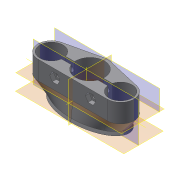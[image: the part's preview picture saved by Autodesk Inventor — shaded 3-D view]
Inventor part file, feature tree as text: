
AUTODESK INVENTOR PART (.ipt)
format: ipt  version: 2015 SP2 (Build 190223200, 223)  size: 519,680 bytes
history: native  units: mm
features: sketch x10, other x6, extrude x6, plane x3, loft x2, mirror x2
ambient origin geometry x8: Origin, YZ Plane, XZ Plane, XY Plane, X Axis, Y Axis, Z Axis, Center Point
bodies: Body1 (feature_tree)
feature tree (29):
  other  "Sólido2"
  extrude  "Extrusión1"  Depth=48.0mm
  extrude  "Extrusión2"  Depth=9.0mm
  extrude  "Extrusión3"  Depth=16.0mm
  extrude  "Extrusión4"  Depth=20.0mm
  plane  "Plano de trabajo3"
  extrude  "Extrusión5"  Depth=13.0mm TaperAngle=0.0deg
  extrude  "Extrusión6"  Depth=3.0mm
  sketch  "Boceto14"  dims[d51=10.0mm d52=10.0mm]
  plane  "Plano de trabajo4"
  loft  "Solevación2"
  mirror  "Simetría2"
  sketch  "Boceto16"  dims[d55=8.5mm]
  plane  "Plano de trabajo5"
  loft  "Solevación4"
  mirror  "Simetría3"
  sketch  "Boceto8"  dims[d36=9.25mm d37=48.0mm]
  sketch  "Boceto9"  dims[d38=15.0mm d39=9.0mm]
  sketch  "Boceto10"  dims[d41=13.0mm d42=0.0mm d43=16.0mm]
  sketch  "Boceto11"  dims[d44=16.0mm d45=20.0mm]
  sketch  "Boceto12"  dims[d46=12.0mm d47=13.0mm d48=0.0mm]
  sketch  "Boceto13"  dims[d49=3.0mm d50=3.0mm]
  sketch  "Boceto15"  dims[d53=1.0mm d54=17.0mm]
  sketch  "Boceto17"  dims[d56=13.0mm d57=0.0mm d58=3.75mm d59=3.75mm d60=24.8mm d61=12.4mm d62=5.5mm d63=13.0mm d64=0.0mm d65=7.2mm d66=7.2mm d67=5.0mm d68=0.0mm d69=6.235mm d70=6.235mm d71=2.8mm d72=0.0mm d74=-10.0mm d75=25.0mm d76=12.5mm d77=26.0mm d78=13.0mm d79=0.0mm d80=90.0deg d81=0.0mm d82=90.0deg d83=0.500016mm d84=0.500055mm d85=-2.0mm d86=27.0mm d87=13.5mm d90=25.0mm d91=12.5mm d96=0.0mm d97=90.0deg d98=0.0mm d99=90.0deg]
  other  "Proyectar aristas de corte3"
  other  "Proyectar aristas de corte4"
  other  "Proyectar aristas de corte5"
  other  "Proyectar aristas de corte6"
  other  "Proyectar aristas de corte7"
